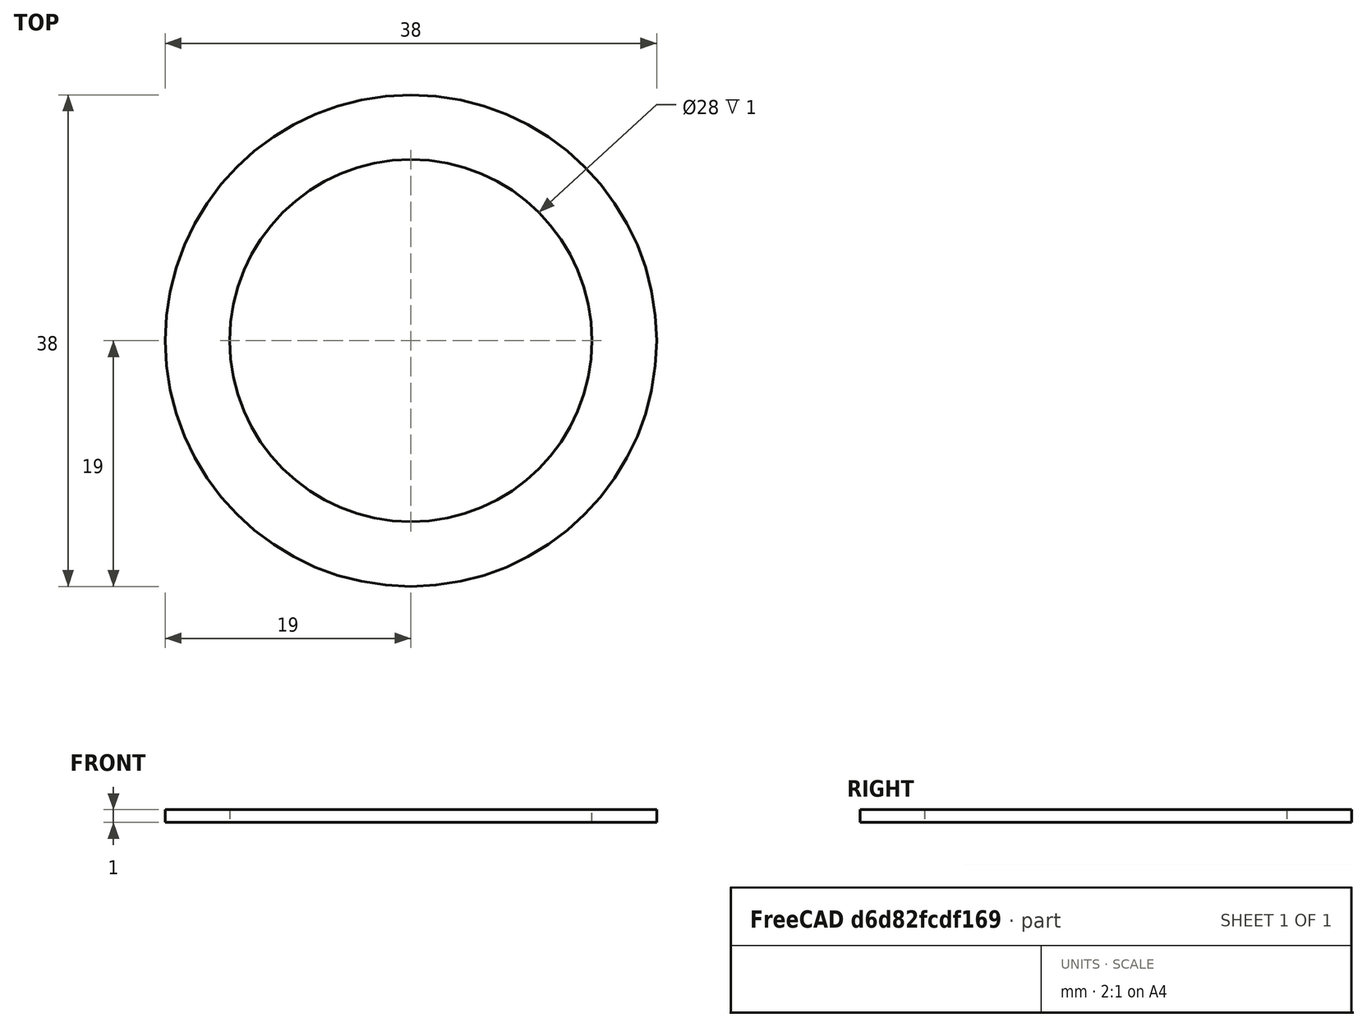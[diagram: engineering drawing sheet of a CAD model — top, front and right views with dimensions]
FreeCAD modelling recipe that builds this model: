
FCSTD DOCUMENT  (FreeCAD 0.19R24276 (Git))
Label: Metki_1
License: All rights reserved
LicenseURL: http://en.wikipedia.org/wiki/All_rights_reserved
objects: Sketcher::SketchObject×2, PartDesign::Pad×1, PartDesign::Body×1
note: 5 computed .brp shape members not serialized (recipe doc carries the construction recipe); baked Part::Feature solids carry a one-line shape summary decoded from their .brp

FEATURE [Sketcher::SketchObject] Sketch
  FullyConstrained = true
  MapMode = 5
  Support = -> [XY_Plane]
  sketch-geometry (2):
    g0: Circle CenterX=0 CenterY=0 CenterZ=0 NormalX=0 NormalY=0 NormalZ=1 AngleXU=0 Radius=19
    g1: Circle CenterX=0 CenterY=0 CenterZ=0 NormalX=0 NormalY=0 NormalZ=1 AngleXU=0 Radius=14
  constraints (4):
    c: Coincident(g0,g-1)
    c: Diameter(g0) = 38
    c: Coincident(g1,g0)
    c: Diameter(g1) = 28
FEATURE [PartDesign::Pad] Pad
  Direction = (1,1,1)
  Length = 1
  Length2 = 100
  Profile = -> Sketch
  Type = 0
FEATURE [Sketcher::SketchObject] Sketch001
  FullyConstrained = false
  MapMode = 5
  Placement = pos=(0,0,1) rot=(0,0,1;0rad)
  Support = -> [Pad]
  sketch-geometry (60):
    g0: LineSegment StartX=0 StartY=0 StartZ=0 EndX=150 EndY=0 EndZ=0
    g1: LineSegment StartX=141 StartY=15.5885 StartZ=0 EndX=141 EndY=-15.5885 EndZ=0
    g2: LineSegment StartX=141 StartY=-15.5885 StartZ=0 EndX=168 EndY=0 EndZ=0
    g3: LineSegment StartX=168 StartY=0 StartZ=0 EndX=141 EndY=15.5885 EndZ=0
    g4: Circle CenterX=150 CenterY=0 CenterZ=0 NormalX=0 NormalY=0 NormalZ=1 AngleXU=0 Radius=18
    g5: Circle CenterX=141 CenterY=15.5885 CenterZ=0 NormalX=0 NormalY=0 NormalZ=1 AngleXU=0 Radius=1.5
    g6: Circle CenterX=168 CenterY=0 CenterZ=0 NormalX=0 NormalY=0 NormalZ=1 AngleXU=0 Radius=1.5
    g7: Circle CenterX=141 CenterY=-15.5885 CenterZ=0 NormalX=0 NormalY=0 NormalZ=1 AngleXU=0 Radius=1.5
    g8: ArcOfCircle CenterX=141 CenterY=15.5885 CenterZ=0 NormalX=0 NormalY=0 NormalZ=1 AngleXU=0 Radius=4 StartAngle=5.62038 EndAngle=11.1348
    g9: ArcOfCircle CenterX=141 CenterY=-15.5885 CenterZ=0 NormalX=0 NormalY=0 NormalZ=1 AngleXU=0 Radius=4 StartAngle=1.43159 EndAngle=6.94599
    g10: ArcOfCircle CenterX=168 CenterY=0 CenterZ=0 NormalX=0 NormalY=0 NormalZ=1 AngleXU=0 Radius=4 StartAngle=3.52599 EndAngle=9.04038
    g11: Circle CenterX=150 CenterY=0 CenterZ=0 NormalX=0 NormalY=0 NormalZ=1 AngleXU=0 Radius=1.5
    g12: ArcOfCircle CenterX=150 CenterY=0 CenterZ=0 NormalX=0 NormalY=0 NormalZ=1 AngleXU=0 Radius=4 StartAngle=0.384397 EndAngle=1.71
    g13: ArcOfCircle CenterX=150 CenterY=0 CenterZ=0 NormalX=0 NormalY=0 NormalZ=1 AngleXU=0 Radius=14 StartAngle=3.28494 EndAngle=4.08144
    g14: ArcOfCircle CenterX=150 CenterY=0 CenterZ=0 NormalX=0 NormalY=0 NormalZ=1 AngleXU=0 Radius=12 StartAngle=4.31412 EndAngle=6.15786
    g15: LineSegment StartX=168 StartY=-1.5 StartZ=0 EndX=167.937 EndY=-1.5 EndZ=0
    g16: LineSegment StartX=150 StartY=-1.5 StartZ=0 EndX=150 EndY=0 EndZ=0
    g17: LineSegment StartX=150 StartY=0 StartZ=0 EndX=150 EndY=1.5 EndZ=0
    g18: LineSegment StartX=142.299 StartY=16.3385 StartZ=0 EndX=142.33 EndY=16.2842 EndZ=0
    g19: LineSegment StartX=139.701 StartY=14.8385 StartZ=0 EndX=139.732 EndY=14.7842 EndZ=0
    g20: LineSegment StartX=148.701 StartY=-0.750001 StartZ=0 EndX=150 EndY=0 EndZ=0
    g21: LineSegment StartX=150 StartY=0 StartZ=0 EndX=151.299 EndY=0.75 EndZ=0
    g22: LineSegment StartX=139.701 StartY=14.8385 StartZ=0 EndX=141 EndY=15.5885 EndZ=0
    g23: LineSegment StartX=141 StartY=15.5885 StartZ=0 EndX=142.299 EndY=16.3385 EndZ=0
    g24: LineSegment StartX=149.445 StartY=-3.96131 StartZ=0 EndX=145.346 EndY=-11.0608 EndZ=0
    g25: LineSegment StartX=141 StartY=-15.5885 StartZ=0 EndX=139.701 EndY=-14.8385 EndZ=0
    g26: LineSegment StartX=141 StartY=-15.5885 StartZ=0 EndX=142.299 EndY=-16.3385 EndZ=0
    g27: LineSegment StartX=151.299 StartY=-0.75 StartZ=0 EndX=150 EndY=0 EndZ=0
    g28: LineSegment StartX=150 StartY=0 StartZ=0 EndX=148.701 EndY=0.75 EndZ=0
    g29: LineSegment StartX=0.0272028 StartY=-2 StartZ=0 EndX=13.8564 EndY=-2 EndZ=0
    g30: LineSegment StartX=146.669 StartY=2 StartZ=0 EndX=138.168 EndY=2 EndZ=0
    g31: ArcOfCircle CenterX=0 CenterY=0 CenterZ=0 NormalX=0 NormalY=0 NormalZ=1 AngleXU=0 Radius=19 StartAngle=0.105459 EndAngle=6.17773
    g32: LineSegment StartX=13.8564 StartY=2 StartZ=0 EndX=-0.0272028 EndY=2 EndZ=0
    g33: LineSegment StartX=18.8944 StartY=-2 StartZ=0 EndX=136.144 EndY=-2 EndZ=0
    g34: LineSegment StartX=136.144 StartY=2 StartZ=0 EndX=18.8944 EndY=2 EndZ=0
    g35: LineSegment StartX=138.168 StartY=-2 StartZ=0 EndX=139.694 EndY=-2 EndZ=0
    g36: LineSegment StartX=142.748 StartY=9.5608 StartZ=0 EndX=146.847 EndY=2.46131 EndZ=0
    g37: LineSegment StartX=145.346 StartY=11.0608 StartZ=0 EndX=149.445 EndY=3.96131 EndZ=0
    g38: LineSegment StartX=163.919 StartY=1.5 StartZ=0 EndX=164.292 EndY=1.5 EndZ=0
    g39: LineSegment StartX=161.906 StartY=-1.5 StartZ=0 EndX=153.708 EndY=-1.5 EndZ=0
    g40: LineSegment StartX=144.339 StartY=-12.8046 StartZ=0 EndX=144.153 EndY=-13.1271 EndZ=0
    g41: LineSegment StartX=142.748 StartY=-9.5608 StartZ=0 EndX=146.847 EndY=-2.46131 EndZ=0
    g42: ArcOfCircle CenterX=150 CenterY=0 CenterZ=0 NormalX=0 NormalY=0 NormalZ=1 AngleXU=0 Radius=14 StartAngle=4.29614 EndAngle=6.17584
    g43: ArcOfCircle CenterX=150 CenterY=0 CenterZ=0 NormalX=0 NormalY=0 NormalZ=1 AngleXU=0 Radius=14 StartAngle=2.20174 EndAngle=2.99825
    g44: LineSegment StartX=144.153 StartY=13.1271 StartZ=0 EndX=144.339 EndY=12.8046 EndZ=0
    g45: LineSegment StartX=141.555 StartY=11.6271 StartZ=0 EndX=141.741 EndY=11.3046 EndZ=0
    g46: LineSegment StartX=141.555 StartY=-11.6271 StartZ=0 EndX=141.741 EndY=-11.3046 EndZ=0
    g47: LineSegment StartX=142.33 StartY=-16.2842 StartZ=0 EndX=142.299 EndY=-16.3385 EndZ=0
    g48: LineSegment StartX=164.292 StartY=-1.5 StartZ=0 EndX=163.919 EndY=-1.5 EndZ=0
    g49: LineSegment StartX=167.937 StartY=1.5 StartZ=0 EndX=168 EndY=1.5 EndZ=0
    g50: ArcOfCircle CenterX=150 CenterY=0 CenterZ=0 NormalX=0 NormalY=0 NormalZ=1 AngleXU=0 Radius=14 StartAngle=0.107349 EndAngle=1.98705
    g51: ArcOfCircle CenterX=150 CenterY=0 CenterZ=0 NormalX=0 NormalY=0 NormalZ=1 AngleXU=0 Radius=12 StartAngle=0.125328 EndAngle=1.96907
    g52: ArcOfCircle CenterX=150 CenterY=0 CenterZ=0 NormalX=0 NormalY=0 NormalZ=1 AngleXU=0 Radius=4 StartAngle=2.47879 EndAngle=3.80439
    g53: ArcOfCircle CenterX=150 CenterY=0 CenterZ=0 NormalX=0 NormalY=0 NormalZ=1 AngleXU=0 Radius=4 StartAngle=4.57319 EndAngle=5.89879
    g54: LineSegment StartX=153.708 StartY=1.5 StartZ=0 EndX=161.906 EndY=1.5 EndZ=0
    g55: ArcOfCircle CenterX=150 CenterY=0 CenterZ=0 NormalX=0 NormalY=0 NormalZ=1 AngleXU=0 Radius=12 StartAngle=2.21972 EndAngle=4.06346
    g56: LineSegment StartX=148.268 StartY=0 StartZ=0 EndX=148.701 EndY=0.75 EndZ=0
    g57: Circle CenterX=0 CenterY=0 CenterZ=0 NormalX=0 NormalY=0 NormalZ=1 AngleXU=0 Radius=14
    g58: LineSegment StartX=150 StartY=0 StartZ=0 EndX=168 EndY=0 EndZ=0
    g59: LineSegment StartX=136.144 StartY=-2 StartZ=0 EndX=136.144 EndY=2 EndZ=0
  constraints (154):
    c: Coincident(g0,g-1)
    c: PointOnObject(g0,g-1)
    c: DistanceX(g0,g0) = 150
    c: Coincident(g1,g2)
    c: Coincident(g2,g3)
    c: Coincident(g3,g1)
    c: Equal(g1,g2)
    c: Equal(g1,g3)
    c: PointOnObject(g1,g4)
    c: PointOnObject(g2,g4)
    c: PointOnObject(g3,g4)
    c: Coincident(g4,g0)
    c: Coincident(g5,g1)
    c: Coincident(g6,g2)
    c: Coincident(g7,g1)
    c: Equal(g7,g5)
    c: Equal(g7,g6)
    c: Coincident(g8,g1)
    c: Coincident(g9,g1)
    c: Coincident(g10,g2)
    c: Diameter(g8) = 8
    c: Equal(g8,g9)
    c: Equal(g8,g10)
    c: Coincident(g11,g0)
    c: Diameter(g11) = 3
    c: Diameter(g7) = 3
    c: Coincident(g12,g11)
    c: Equal(g8,g12)
    c: Coincident(g13,g11)
    c: Diameter(g13) = 28
    c: Coincident(g14,g11)
    c: Diameter(g14) = 24
    c: Diameter(g4) = 36
    c: PointOnObject(g15,g6)
    c: PointOnObject(g16,g11)
    c: Tangent(g15,g6)
    c: PointOnObject(g17,g11)
    c: PointOnObject(g49,g6)
    c: Coincident(g16,g11)
    c: Coincident(g17,g11)
    c: Vertical(g17)
    c: Perpendicular(g16,g15)
    c: PointOnObject(g18,g5)
    c: Tangent(g18,g11)
    c: PointOnObject(g19,g5)
    c: PointOnObject(g20,g11)
    c: Tangent(g19,g11)
    c: Coincident(g20,g11)
    c: Coincident(g21,g11)
    c: Coincident(g22,g19)
    c: Coincident(g22,g5)
    c: Coincident(g23,g5)
    c: Coincident(g23,g18)
    c: Perpendicular(g19,g22)
    c: Perpendicular(g18,g23)
    c: PointOnObject(g25,g7)
    c: PointOnObject(g56,g11)
    c: PointOnObject(g27,g11)
    c: PointOnObject(g47,g7)
    c: Tangent(g24,g7)
    c: Coincident(g25,g7)
    c: Coincident(g26,g7)
    c: Coincident(g26,g47)
    c: Coincident(g27,g11)
    c: Perpendicular(g27,g24)
    c: Coincident(g28,g11)
    c: Coincident(g28,g56)
    c: Perpendicular(g18,g21)
    c: Horizontal(g29)
    c: Horizontal(g30)
    c: Symmetric(g29,g32,g-1)
    c: DistanceY(g29,g32) = 4
    c: Coincident(g31,g-1)
    c: Diameter(g31) = 38
    c: Coincident(g34,g31)
    c: Tangent(g30,g32)
    c: Coincident(g33,g31)
    c: Tangent(g29,g33)
    c: PointOnObject(g30,g14)
    c: Coincident(g34,g43)
    c: Tangent(g30,g34)
    c: Coincident(g33,g13)
    c: PointOnObject(g35,g14)
    c: Tangent(g33,g35)
    c: PointOnObject(g45,g13)
    c: PointOnObject(g36,g14)
    c: Tangent(g19,g36)
    c: PointOnObject(g44,g13)
    c: PointOnObject(g37,g14)
    c: Tangent(g18,g37)
    c: PointOnObject(g38,g13)
    c: PointOnObject(g48,g13)
    c: Tangent(g15,g39)
    c: PointOnObject(g40,g13)
    c: Tangent(g24,g40)
    c: Equal(g13,g42)
    c: Coincident(g13,g46)
    c: Coincident(g13,g42)
    c: PointOnObject(g42,g40)
    c: Coincident(g14,g24)
    c: Coincident(g55,g41)
    c: Equal(g42,g43)
    c: PointOnObject(g50,g18)
    c: Coincident(g42,g43)
    c: PointOnObject(g43,g19)
    c: PointOnObject(g8,g18)
    c: PointOnObject(g8,g19)
    c: PointOnObject(g18,g4)
    c: Tangent(g18,g44)
    c: PointOnObject(g19,g4)
    c: Tangent(g19,g45)
    c: PointOnObject(g45,g8)
    c: PointOnObject(g44,g8)
    c: Coincident(g46,g9)
    c: PointOnObject(g47,g4)
    c: Tangent(g40,g47)
    c: Coincident(g40,g9)
    c: PointOnObject(g15,g4)
    c: Tangent(g15,g48)
    c: PointOnObject(g49,g4)
    c: Tangent(g38,g49)
    c: Coincident(g10,g48)
    c: Equal(g42,g50)
    c: PointOnObject(g42,g48)
    c: Coincident(g42,g50)
    c: PointOnObject(g50,g38)
    c: Coincident(g10,g38)
    c: Equal(g14,g51)
    c: Coincident(g14,g39)
    c: Coincident(g51,g54)
    c: Coincident(g14,g51)
    c: Equal(g12,g52)
    c: Coincident(g12,g52)
    c: Equal(g52,g53)
    c: Coincident(g52,g53)
    c: Coincident(g54,g12)
    c: Coincident(g37,g12)
    c: Coincident(g36,g52)
    c: Equal(g51,g55)
    c: PointOnObject(g51,g37)
    c: PointOnObject(g55,g36)
    c: Coincident(g51,g55)
    c: Coincident(g24,g53)
    c: Coincident(g41,g52)
    c: PointOnObject(g56,g0)
    c: Tangent(g41,g56)
    c: Coincident(g39,g53)
    c: Coincident(g57,g31)
    c: Diameter(g57) = 28
    c: Coincident(g58,g11)
    c: Coincident(g58,g6)
    c: Horizontal(g58)
    c: Coincident(g59,g13)
    c: Coincident(g59,g34)
FEATURE [PartDesign::Body] Body
  Group = -> [Sketch,Pad,Sketch001]
  Origin = -> Origin
  Tip = -> Pad
